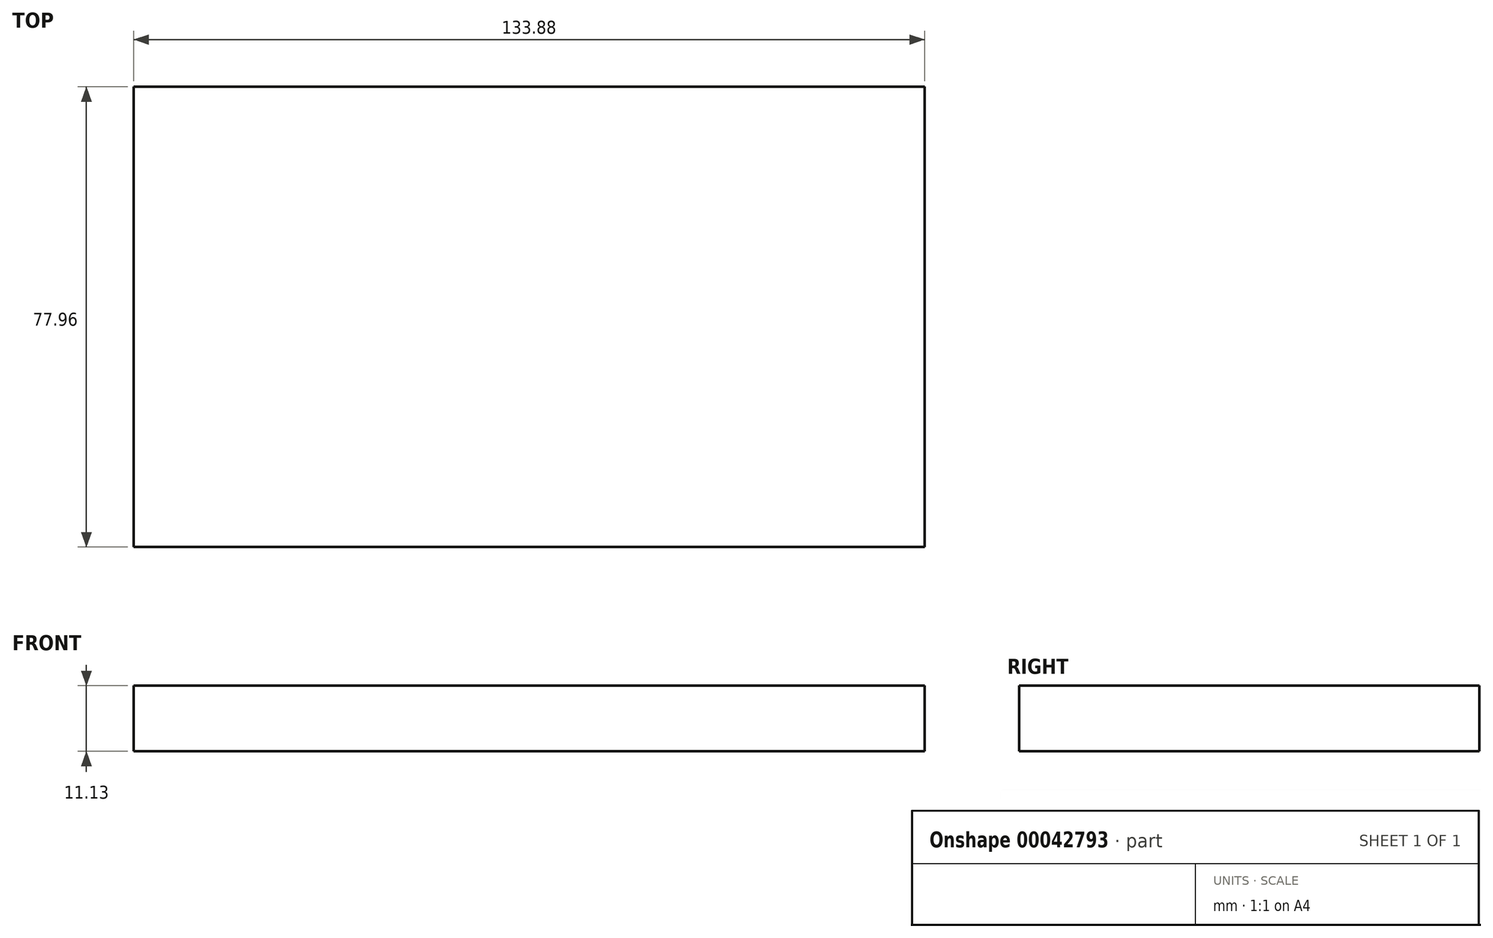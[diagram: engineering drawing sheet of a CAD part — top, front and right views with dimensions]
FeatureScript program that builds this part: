
annotation { "Feature Type Name" : "Feature", "Feature Type Description" : "" }
export const myFeature = defineFeature(function(context is Context, id is Id, definition is map)
    precondition{}
    {
        {
            var Q0;
            Q0=qCreatedBy(makeId("Top.planeOp"),FACE);
            var sketch = newSketch(context, id + "F0", { "sketchPlane" : qUnion([Q0])});
            skLineSegment(sketch, "E0.rect.bottom", {"start": v(-66.94, 38.98) * mm, "end": v(66.94, 38.98) * mm});
            skLineSegment(sketch, "E0.rect.top", {"start": v(-66.94, -38.98) * mm, "end": v(66.94, -38.98) * mm});
            skLineSegment(sketch, "E0.rect.left", {"start": v(-66.94, 38.98) * mm, "end": v(-66.94, -38.98) * mm});
            skLineSegment(sketch, "E0.rect.right", {"start": v(66.94, 38.98) * mm, "end": v(66.94, -38.98) * mm});
            skPoint(sketch, "E0.rect.middle", {"position": v(0, 0) * mm});
            skSolve(sketch);
        }
        {
            var Q0;
            Q0=makeQuery(id+"F0.imprint","IMPRINT",FACE,{"disambiguationData":[TD([[makeQuery(id+"F0.imprint","IMPRINT",EDGE,{"derivedFrom":sQuery(id+"F0.wireOp",EDGE,"E0.rect.bottom")}),-1.0]])]});
            extrude(context, id + "F1", {"entities" : qUnion([Q0]), "depth" : 11.13 * mm});
        }
    });
